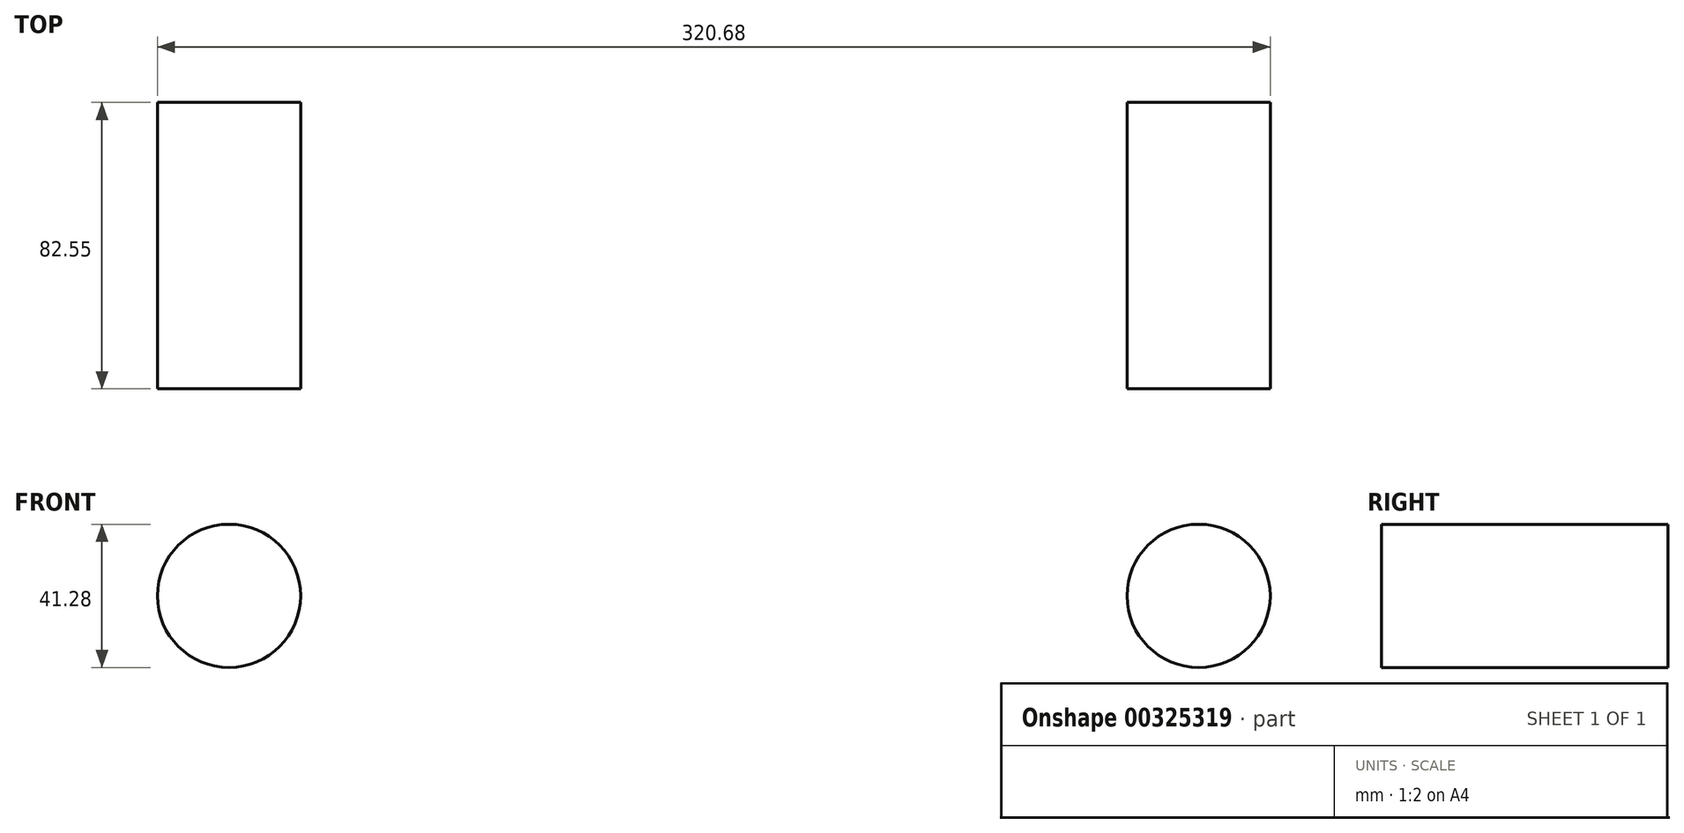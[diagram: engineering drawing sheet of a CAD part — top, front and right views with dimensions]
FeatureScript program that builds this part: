
annotation { "Feature Type Name" : "Feature", "Feature Type Description" : "" }
export const myFeature = defineFeature(function(context is Context, id is Id, definition is map)
    precondition{}
    {
        {
            var Q0;
            Q0=qCreatedBy(makeId("Top.planeOp"),FACE);
            var sketch = newSketch(context, id + "F0", { "sketchPlane" : qUnion([Q0])});
            skLineSegment(sketch, "E0", {"start": v(279.4, -82.55) * mm, "end": v(279.4, 0) * mm});
            skLineSegment(sketch, "E1", {"start": v(0, -82.55) * mm, "end": v(0, 0) * mm});
            skLineSegment(sketch, "E2.bottom", {"start": v(33.02, 53.95) * mm, "end": v(248.92, 53.95) * mm});
            skLineSegment(sketch, "E2.top", {"start": v(33.02, -95.25) * mm, "end": v(248.92, -95.25) * mm});
            skLineSegment(sketch, "E2.left", {"start": v(33.02, 53.95) * mm, "end": v(33.02, -95.25) * mm});
            skLineSegment(sketch, "E2.right", {"start": v(248.92, 53.95) * mm, "end": v(248.92, -95.25) * mm});
            skLineSegment(sketch, "E3.bottom", {"start": v(77.47, -361.95) * mm, "end": v(204.47, -361.95) * mm});
            skLineSegment(sketch, "E3.top", {"start": v(77.47, -480.47) * mm, "end": v(204.47, -480.47) * mm});
            skLineSegment(sketch, "E3.left", {"start": v(77.47, -361.95) * mm, "end": v(77.47, -480.47) * mm});
            skLineSegment(sketch, "E3.right", {"start": v(204.47, -361.95) * mm, "end": v(204.47, -480.47) * mm});
            skArc(sketch, "E4", {"start": v(279.4, -82.55) * mm, "mid": v(260.8, -127.45) * mm, "end": v(215.9, -146.05) * mm});
            skLineSegment(sketch, "E5", {"start": v(216.15, -146.05) * mm, "end": v(215.9, -146.05) * mm});
            skArc(sketch, "E6", {"start": v(216.15, -146.05) * mm, "mid": v(162.27, -168.37) * mm, "end": v(139.95, -222.25) * mm});
            skLineSegment(sketch, "E7", {"start": v(139.95, -222.25) * mm, "end": v(139.95, -229.56) * mm});
            skArc(sketch, "E8", {"start": v(139.95, -229.56) * mm, "mid": v(117.64, -283.44) * mm, "end": v(63.75, -305.76) * mm});
            skLineSegment(sketch, "E9", {"start": v(63.75, -305.76) * mm, "end": v(51.05, -305.76) * mm});
            skArc(sketch, "E10", {"start": v(51.05, -305.76) * mm, "mid": v(-2.83, -328.07) * mm, "end": v(-25.15, -381.96) * mm});
            skArc(sketch, "E11", {"start": v(0, -82.55) * mm, "mid": v(18.6, -127.45) * mm, "end": v(63.5, -146.05) * mm});
            skLineSegment(sketch, "E12", {"start": v(63.5, -146.05) * mm, "end": v(63.75, -146.05) * mm});
            skArc(sketch, "E13", {"start": v(63.75, -146.05) * mm, "mid": v(117.64, -168.37) * mm, "end": v(139.95, -222.25) * mm});
            skLineSegment(sketch, "E14", {"start": v(-25.15, -381.96) * mm, "end": v(-25.15, -445.46) * mm});
            skPoint(sketch, "E15", {"position": v(140.97, 53.95) * mm});
            skPoint(sketch, "E16", {"position": v(140.97, -480.47) * mm});
            skLineSegment(sketch, "E17.bottom", {"start": v(-19.05, 53.76) * mm, "end": v(19.05, 53.76) * mm});
            skLineSegment(sketch, "E17.top", {"start": v(-19.05, -31.75) * mm, "end": v(19.05, -31.75) * mm});
            skLineSegment(sketch, "E17.left", {"start": v(-19.05, 53.76) * mm, "end": v(-19.05, -31.75) * mm});
            skLineSegment(sketch, "E17.right", {"start": v(19.05, 53.76) * mm, "end": v(19.05, -31.75) * mm});
            skPoint(sketch, "E18", {"position": v(0, 53.76) * mm});
            skLineSegment(sketch, "E19.bottom", {"start": v(260.35, 52.8) * mm, "end": v(298.45, 52.8) * mm});
            skLineSegment(sketch, "E19.top", {"start": v(260.35, -44.45) * mm, "end": v(298.45, -44.45) * mm});
            skLineSegment(sketch, "E19.left", {"start": v(260.35, 52.8) * mm, "end": v(260.35, -44.45) * mm});
            skLineSegment(sketch, "E19.right", {"start": v(298.45, 52.8) * mm, "end": v(298.45, -44.45) * mm});
            skPoint(sketch, "E20", {"position": v(279.4, 52.8) * mm});
            skLineSegment(sketch, "E21", {"start": v(0, 0) * mm, "end": v(0, 53.76) * mm});
            skLineSegment(sketch, "E22", {"start": v(0, 0) * mm, "end": v(0, -31.75) * mm});
            skLineSegment(sketch, "E23", {"start": v(279.4, 0) * mm, "end": v(279.4, 52.8) * mm});
            skLineSegment(sketch, "E24", {"start": v(279.4, 0) * mm, "end": v(279.4, -44.45) * mm});
            skSolve(sketch);
        }
        {
            var Q0;
            Q0=qCreatedBy(makeId("Front.planeOp"),FACE);
            var sketch = newSketch(context, id + "F1", { "sketchPlane" : qUnion([Q0])});
            skCircle(sketch, "E25", {"center": v(279.4, 0) * mm, "radius": 20.64 * mm});
            skCircle(sketch, "E26", {"center": v(0, 0) * mm, "radius": 20.64 * mm});
            skSolve(sketch);
        }
        {
            var Q0;
            Q0=qSketchRegion(id+"F1",true);
            var Q1;
            Q1=sQuery(id+"F1.wireOp",EDGE,"E25");
            var Q2;
            Q2=sQuery(id+"F0.wireOp",EDGE,"E0");
            sweep(context, id + "F2", {"bodyType" : ToolBodyType.SURFACE, "profiles" : qUnion([Q0]), "surfaceProfiles" : qUnion([Q1]), "path" : qUnion([Q2])});
        }
        {
            var Q0;
            Q0=sQuery(id+"F0.wireOp",VERTEX,"E5.start");
            var Q1;
            Q1=qCreatedBy(makeId("Right.planeOp"),FACE);
            cPlane(context, id + "F3", {"entities" : qUnion([Q0, Q1]), "cplaneType" : CPlaneType.PLANE_POINT, "offset" : 25.4 * mm, "width" : 152.4 * mm, "height" : 152.4 * mm});
        }
        {
            var Q0;
            Q0=qCreatedBy(id+"F3.planeOp",FACE);
            var sketch = newSketch(context, id + "F4", { "sketchPlane" : qUnion([Q0])});
            skCircle(sketch, "E27", {"center": v(-146.05, 0) * mm, "radius": 22.23 * mm});
            skSolve(sketch);
        }
        {
            var Q0;
            Q0=sQuery(id+"F0.wireOp",VERTEX,"E6.end");
            var Q1;
            Q1=qCreatedBy(makeId("Front.planeOp"),FACE);
            cPlane(context, id + "F5", {"entities" : qUnion([Q0, Q1]), "cplaneType" : CPlaneType.PLANE_POINT, "offset" : 25.4 * mm, "width" : 152.4 * mm, "height" : 152.4 * mm});
        }
        {
            var Q0;
            Q0=qCreatedBy(id+"F5.planeOp",FACE);
            var sketch = newSketch(context, id + "F6", { "sketchPlane" : qUnion([Q0])});
            skCircle(sketch, "E28", {"center": v(139.95, 0) * mm, "radius": 23.81 * mm});
            skSolve(sketch);
        }
        {
            var Q0;
            Q0=sQuery(id+"F0.wireOp",VERTEX,"E9.end");
            var Q1;
            Q1=qCreatedBy(makeId("Right.planeOp"),FACE);
            cPlane(context, id + "F7", {"entities" : qUnion([Q0, Q1]), "cplaneType" : CPlaneType.PLANE_POINT, "offset" : 25.4 * mm, "width" : 152.4 * mm, "height" : 152.4 * mm});
        }
        {
            var Q0;
            Q0=qCreatedBy(id+"F7.planeOp",FACE);
            var sketch = newSketch(context, id + "F8", { "sketchPlane" : qUnion([Q0])});
            skCircle(sketch, "E29", {"center": v(-305.76, 0) * mm, "radius": 25.4 * mm});
            skSolve(sketch);
        }
        {
            var Q0;
            Q0=qSketchRegion(id+"F1",true);
            var Q1;
            Q1=sQuery(id+"F1.wireOp",EDGE,"E26");
            var Q2;
            Q2=sQuery(id+"F0.wireOp",EDGE,"E1");
            sweep(context, id + "F9", {"bodyType" : ToolBodyType.SURFACE, "profiles" : qUnion([Q0]), "surfaceProfiles" : qUnion([Q1]), "path" : qUnion([Q2])});
        }
        {
            var Q0;
            Q0=sQuery(id+"F0.wireOp",VERTEX,"E12.start");
            var Q1;
            Q1=qCreatedBy(makeId("Right.planeOp"),FACE);
            cPlane(context, id + "F10", {"entities" : qUnion([Q0, Q1]), "cplaneType" : CPlaneType.PLANE_POINT, "offset" : 25.4 * mm, "width" : 152.4 * mm, "height" : 152.4 * mm});
        }
        {
            var Q0;
            Q0=qCreatedBy(id+"F10.planeOp",FACE);
            var sketch = newSketch(context, id + "F11", { "sketchPlane" : qUnion([Q0])});
            skCircle(sketch, "E30", {"center": v(-146.05, 0) * mm, "radius": 22.22 * mm});
            skSolve(sketch);
        }
        {
            var Q0;
            Q0=qCreatedBy(makeId("Front.planeOp"),FACE);
            var sketch = newSketch(context, id + "F12", { "sketchPlane" : qUnion([Q0])});
            skCircle(sketch, "E31", {"center": v(0, 0) * mm, "radius": 19.05 * mm});
            skCircle(sketch, "E32", {"center": v(279.4, 0) * mm, "radius": 19.05 * mm});
            skSolve(sketch);
        }
    });
